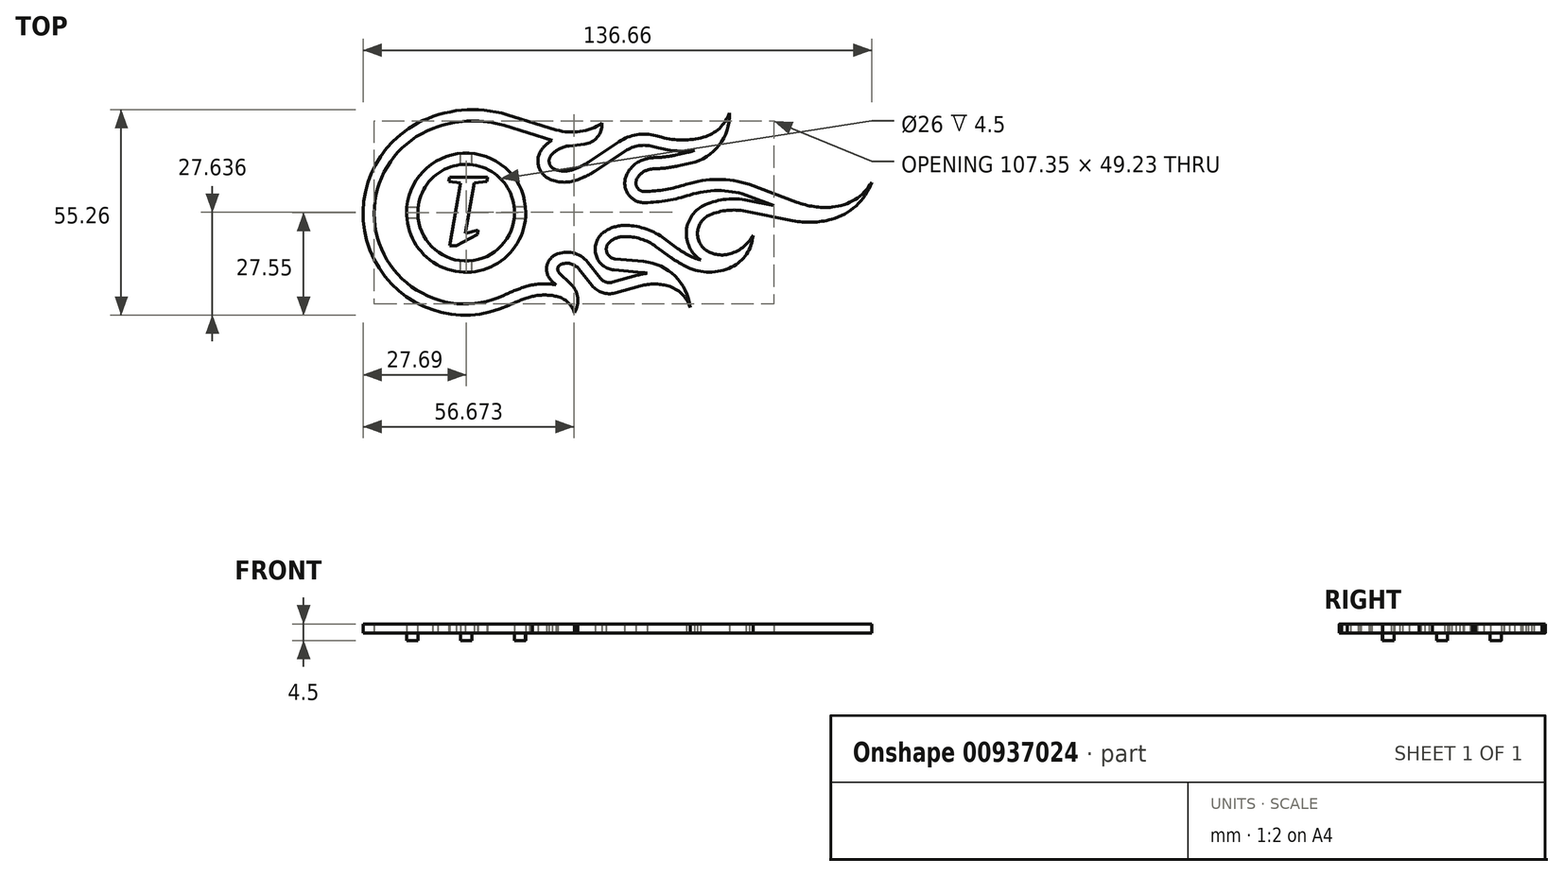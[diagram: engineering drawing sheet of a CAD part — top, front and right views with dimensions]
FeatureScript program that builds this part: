
annotation { "Feature Type Name" : "Feature", "Feature Type Description" : "" }
export const myFeature = defineFeature(function(context is Context, id is Id, definition is map)
    precondition{}
    {
        {
            var Q0;
            Q0=qCreatedBy(makeId("Top.planeOp"),FACE);
            cPlane(context, id + "F0", {"entities" : qUnion([Q0]), "cplaneType" : CPlaneType.OFFSET, "offset" : 2 * mm, "width" : 150 * mm, "height" : 150 * mm});
        }
        {
            var Q0;
            Q0=qCreatedBy(id+"F0.planeOp",FACE);
            var sketch = newSketch(context, id + "F1", { "sketchPlane" : qUnion([Q0])});
            skArc(sketch, "E0", {"start": v(-15.8, 20.8) * mm, "mid": v(-9.44, 20.3) * mm, "end": v(-3.49, 22.58) * mm});
            skLineSegment(sketch, "E1", {"start": v(-29, 24.82) * mm, "end": v(-15.8, 20.8) * mm});
            skArc(sketch, "E2", {"start": v(-53.14, 22.5) * mm, "mid": v(-64.76, -14.01) * mm, "end": v(-28.48, -26.36) * mm});
            skArc(sketch, "E3", {"start": v(-29, 24.82) * mm, "mid": v(-41.3, 26.06) * mm, "end": v(-53.14, 22.5) * mm});
            skArc(sketch, "E4", {"start": v(-8.25, 16.94) * mm, "mid": v(-4.75, 18.81) * mm, "end": v(-3.49, 22.58) * mm});
            skArc(sketch, "E5", {"start": v(-10.87, -28.44) * mm, "mid": v(-12.7, -25.58) * mm, "end": v(-15.7, -24) * mm});
            skArc(sketch, "E6", {"start": v(-15.7, -24) * mm, "mid": v(-18.94, -23.64) * mm, "end": v(-22.18, -24) * mm});
            skArc(sketch, "E7", {"start": v(-22.18, -24) * mm, "mid": v(-25.39, -25.04) * mm, "end": v(-28.48, -26.36) * mm});
            skArc(sketch, "E8", {"start": v(-10.87, -28.44) * mm, "mid": v(-10.04, -24.35) * mm, "end": v(-11.9, -20.62) * mm});
            skArc(sketch, "E9", {"start": v(-14.69, -15.51) * mm, "mid": v(-15.4, -16.45) * mm, "end": v(-15.02, -17.57) * mm});
            skLineSegment(sketch, "E10", {"start": v(-11.9, -20.62) * mm, "end": v(-15.02, -17.57) * mm});
            skArc(sketch, "E11", {"start": v(-9.7, -16.65) * mm, "mid": v(-12, -15.2) * mm, "end": v(-14.69, -15.51) * mm});
            skLineSegment(sketch, "E12", {"start": v(-9.7, -16.65) * mm, "end": v(-6.22, -21.05) * mm});
            skArc(sketch, "E13", {"start": v(-6.22, -21.05) * mm, "mid": v(-3.42, -23) * mm, "end": v(0, -23.09) * mm});
            skLineSegment(sketch, "E14", {"start": v(-8.25, 16.94) * mm, "end": v(-12.34, 16.47) * mm});
            skArc(sketch, "E15", {"start": v(-12.34, 16.47) * mm, "mid": v(-14.96, 15.66) * mm, "end": v(-17.12, 13.97) * mm});
            skArc(sketch, "E16", {"start": v(-17.12, 13.97) * mm, "mid": v(-17.66, 11.88) * mm, "end": v(-16.27, 10.22) * mm});
            skArc(sketch, "E17", {"start": v(-16.27, 10.22) * mm, "mid": v(-13.63, 9.69) * mm, "end": v(-10.98, 10.22) * mm});
            skLineSegment(sketch, "E18", {"start": v(-10.98, 10.22) * mm, "end": v(-9.42, 10.88) * mm});
            skLineSegment(sketch, "E19", {"start": v(1.1, 17.58) * mm, "end": v(-6.91, 12.23) * mm});
            skArc(sketch, "E20.filletArc", {"start": v(-9.42, 10.88) * mm, "mid": v(-8.13, 11.5) * mm, "end": v(-6.91, 12.23) * mm});
            skArc(sketch, "E21", {"start": v(10.9, 19.2) * mm, "mid": v(5.82, 19.45) * mm, "end": v(1.1, 17.58) * mm});
            skLineSegment(sketch, "E22", {"start": v(10.9, 19.2) * mm, "end": v(12.5, 18.78) * mm});
            skArc(sketch, "E23", {"start": v(12.5, 18.78) * mm, "mid": v(18.13, 18.04) * mm, "end": v(23.76, 18.78) * mm});
            skArc(sketch, "E24", {"start": v(23.76, 18.78) * mm, "mid": v(28.06, 21.17) * mm, "end": v(30.72, 25.31) * mm});
            skArc(sketch, "E25", {"start": v(20.3, 11.8) * mm, "mid": v(27.98, 16.65) * mm, "end": v(30.72, 25.31) * mm});
            skLineSegment(sketch, "E26", {"start": v(20.3, 11.8) * mm, "end": v(16.86, 11.06) * mm});
            skArc(sketch, "E27", {"start": v(10.82, 10.32) * mm, "mid": v(13.86, 10.55) * mm, "end": v(16.86, 11.06) * mm});
            skArc(sketch, "E28", {"start": v(10.82, 10.32) * mm, "mid": v(9.84, 10.23) * mm, "end": v(8.87, 10.03) * mm});
            skArc(sketch, "E29", {"start": v(8.87, 10.03) * mm, "mid": v(7.03, 9.04) * mm, "end": v(5.8, 7.34) * mm});
            skArc(sketch, "E30", {"start": v(5.8, 7.34) * mm, "mid": v(6.02, 5.16) * mm, "end": v(7.97, 4.17) * mm});
            skArc(sketch, "E31", {"start": v(19.12, 6.1) * mm, "mid": v(13.61, 4.74) * mm, "end": v(7.97, 4.17) * mm});
            skArc(sketch, "E32", {"start": v(36.14, 6.1) * mm, "mid": v(27.63, 7.44) * mm, "end": v(19.12, 6.1) * mm});
            skLineSegment(sketch, "E33", {"start": v(0, -23.09) * mm, "end": v(6.9, -21.19) * mm});
            skArc(sketch, "E34", {"start": v(14.19, -21.19) * mm, "mid": v(10.54, -20.7) * mm, "end": v(6.9, -21.19) * mm});
            skArc(sketch, "E35", {"start": v(20.17, -27.02) * mm, "mid": v(17.93, -23.33) * mm, "end": v(14.19, -21.19) * mm});
            skArc(sketch, "E36", {"start": v(20.17, -27.02) * mm, "mid": v(16.15, -18.57) * mm, "end": v(7.68, -14.62) * mm});
            skLineSegment(sketch, "E37", {"start": v(7.68, -14.62) * mm, "end": v(0, -13.91) * mm});
            skArc(sketch, "E38", {"start": v(-1.39, -9.32) * mm, "mid": v(-2.24, -12.08) * mm, "end": v(0, -13.91) * mm});
            skArc(sketch, "E39", {"start": v(2.46, -7.92) * mm, "mid": v(0.42, -8.3) * mm, "end": v(-1.39, -9.32) * mm});
            skArc(sketch, "E40", {"start": v(10.98, -10.59) * mm, "mid": v(6.94, -8.56) * mm, "end": v(2.46, -7.92) * mm});
            skLineSegment(sketch, "E41", {"start": v(10.98, -10.59) * mm, "end": v(15.06, -13.54) * mm});
            skArc(sketch, "E42", {"start": v(15.06, -13.54) * mm, "mid": v(17.16, -14.93) * mm, "end": v(19.37, -16.1) * mm});
            skArc(sketch, "E43", {"start": v(19.37, -16.1) * mm, "mid": v(25.34, -17.46) * mm, "end": v(31.3, -16.1) * mm});
            skArc(sketch, "E44", {"start": v(31.3, -16.1) * mm, "mid": v(35.34, -12.64) * mm, "end": v(37.05, -7.6) * mm});
            skArc(sketch, "E45", {"start": v(30.4, -12.7) * mm, "mid": v(34.29, -10.88) * mm, "end": v(37.05, -7.6) * mm});
            skArc(sketch, "E46", {"start": v(24.84, -11.81) * mm, "mid": v(27.53, -12.78) * mm, "end": v(30.4, -12.7) * mm});
            skArc(sketch, "E47", {"start": v(25.48, -2.1) * mm, "mid": v(22.17, -6.76) * mm, "end": v(24.84, -11.81) * mm});
            skArc(sketch, "E48", {"start": v(35.02, -1.1) * mm, "mid": v(30.17, -0.88) * mm, "end": v(25.48, -2.1) * mm});
            skLineSegment(sketch, "E49", {"start": v(35.02, -1.1) * mm, "end": v(47.7, -3.63) * mm});
            skArc(sketch, "E50", {"start": v(47.7, -3.63) * mm, "mid": v(52.94, -4.06) * mm, "end": v(58.13, -3.3) * mm});
            skArc(sketch, "E51", {"start": v(58.13, -3.3) * mm, "mid": v(64.79, 0.34) * mm, "end": v(68.97, 6.67) * mm});
            skArc(sketch, "E52", {"start": v(58.36, 0) * mm, "mid": v(64.48, 2.05) * mm, "end": v(68.97, 6.67) * mm});
            skArc(sketch, "E53", {"start": v(48.76, 1.34) * mm, "mid": v(53.49, 0.13) * mm, "end": v(58.36, 0) * mm});
            skLineSegment(sketch, "E54", {"start": v(36.14, 6.1) * mm, "end": v(48.76, 1.34) * mm});
            skArc(sketch, "E55.0", {"start": v(-29.87, 21.95) * mm, "mid": v(-38.73, 23.2) * mm, "end": v(-47.54, 21.67) * mm});
            skArc(sketch, "E56", {"start": v(-48.94, 21.12) * mm, "mid": v(-62.73, -11.25) * mm, "end": v(-29.8, -23.67) * mm});
            skLineSegment(sketch, "E57", {"start": v(-48.94, 21.12) * mm, "end": v(-47.54, 21.67) * mm});
            skLineSegment(sketch, "E58.0", {"start": v(-29.87, 21.95) * mm, "end": v(-16.92, 18) * mm});
            skArc(sketch, "E59.0", {"start": v(-12.68, 19.45) * mm, "mid": v(-12.7, 19.44) * mm, "end": v(-12.72, 19.44) * mm});
            skLineSegment(sketch, "E60", {"start": v(-16.92, 18) * mm, "end": v(-16.92, 18) * mm});
            skArc(sketch, "E61", {"start": v(-16.92, 18) * mm, "mid": v(-18.2, 17.08) * mm, "end": v(-19.34, 15.99) * mm});
            skArc(sketch, "E62.0", {"start": v(-19.37, 15.96) * mm, "mid": v(-20.58, 11.21) * mm, "end": v(-17.43, 7.46) * mm});
            skArc(sketch, "E63.0", {"start": v(-17.43, 7.46) * mm, "mid": v(-13.63, 6.69) * mm, "end": v(-9.82, 7.46) * mm});
            skLineSegment(sketch, "E64.0", {"start": v(-9.82, 7.46) * mm, "end": v(-8.25, 8.12) * mm});
            skArc(sketch, "E65.0", {"start": v(-8.25, 8.12) * mm, "mid": v(-6.71, 8.86) * mm, "end": v(-5.25, 9.74) * mm});
            skLineSegment(sketch, "E66.0", {"start": v(2.76, 15.09) * mm, "end": v(-5.25, 9.74) * mm});
            skArc(sketch, "E67.0", {"start": v(10.13, 16.3) * mm, "mid": v(6.31, 16.5) * mm, "end": v(2.76, 15.09) * mm});
            skLineSegment(sketch, "E68.0", {"start": v(10.13, 16.3) * mm, "end": v(11.74, 15.88) * mm});
            skArc(sketch, "E69.0", {"start": v(11.74, 15.88) * mm, "mid": v(16.51, 15.1) * mm, "end": v(21.35, 15.25) * mm});
            skLineSegment(sketch, "E70.0", {"start": v(19.3, 14.65) * mm, "end": v(16.22, 13.99) * mm});
            skArc(sketch, "E71.0", {"start": v(19.66, 14.73) * mm, "mid": v(20.52, 14.95) * mm, "end": v(21.35, 15.25) * mm});
            skArc(sketch, "E72.0", {"start": v(10.73, 13.32) * mm, "mid": v(13.5, 13.53) * mm, "end": v(16.22, 13.99) * mm});
            skArc(sketch, "E73.0", {"start": v(10.73, 13.32) * mm, "mid": v(9.4, 13.2) * mm, "end": v(8.08, 12.92) * mm});
            skArc(sketch, "E74.0", {"start": v(8.08, 12.92) * mm, "mid": v(5.05, 11.3) * mm, "end": v(3.04, 8.52) * mm});
            skArc(sketch, "E75.0", {"start": v(3.04, 8.52) * mm, "mid": v(3.54, 3.47) * mm, "end": v(8.07, 1.17) * mm});
            skArc(sketch, "E76.0", {"start": v(20.04, 3.25) * mm, "mid": v(14.12, 1.79) * mm, "end": v(8.07, 1.17) * mm});
            skLineSegment(sketch, "E77.0", {"start": v(35.6, 1.84) * mm, "end": v(42.66, 0.43) * mm});
            skArc(sketch, "E78.0", {"start": v(35.6, 1.84) * mm, "mid": v(29.87, 2.1) * mm, "end": v(24.3, 0.67) * mm});
            skArc(sketch, "E79.0", {"start": v(24.3, 0.67) * mm, "mid": v(19.19, -6.38) * mm, "end": v(23, -14.2) * mm});
            skArc(sketch, "E80.0", {"start": v(20.66, -13.4) * mm, "mid": v(21.81, -13.87) * mm, "end": v(23, -14.2) * mm});
            skArc(sketch, "E81.0", {"start": v(16.82, -11.12) * mm, "mid": v(18.69, -12.35) * mm, "end": v(20.66, -13.4) * mm});
            skLineSegment(sketch, "E82.0", {"start": v(12.74, -8.16) * mm, "end": v(16.82, -11.12) * mm});
            skArc(sketch, "E83.0", {"start": v(12.74, -8.16) * mm, "mid": v(7.83, -5.7) * mm, "end": v(2.4, -4.92) * mm});
            skArc(sketch, "E84.0", {"start": v(2.4, -4.92) * mm, "mid": v(-0.61, -5.48) * mm, "end": v(-3.28, -7) * mm});
            skArc(sketch, "E85.0", {"start": v(-3.28, -7) * mm, "mid": v(-5.11, -12.95) * mm, "end": v(-0.28, -16.9) * mm});
            skLineSegment(sketch, "E86.0", {"start": v(7.4, -17.6) * mm, "end": v(-0.28, -16.9) * mm});
            skLineSegment(sketch, "E87.0", {"start": v(-0.8, -20.2) * mm, "end": v(6.1, -18.3) * mm});
            skArc(sketch, "E88", {"start": v(8.67, -17.8) * mm, "mid": v(8.04, -17.68) * mm, "end": v(7.4, -17.6) * mm});
            skArc(sketch, "E89", {"start": v(8.67, -17.8) * mm, "mid": v(7.38, -18) * mm, "end": v(6.1, -18.3) * mm});
            skArc(sketch, "E90.0", {"start": v(-3.87, -19.2) * mm, "mid": v(-2.48, -20.16) * mm, "end": v(-0.8, -20.2) * mm});
            skLineSegment(sketch, "E91.0", {"start": v(-7.35, -14.8) * mm, "end": v(-3.87, -19.2) * mm});
            skArc(sketch, "E92.0", {"start": v(-7.35, -14.8) * mm, "mid": v(-11.32, -12.28) * mm, "end": v(-16, -12.81) * mm});
            skArc(sketch, "E93.0", {"start": v(-16, -12.81) * mm, "mid": v(-18.35, -15.97) * mm, "end": v(-17.12, -19.72) * mm});
            skLineSegment(sketch, "E94.0", {"start": v(-15.9, -20.9) * mm, "end": v(-17.12, -19.72) * mm});
            skArc(sketch, "E95.0", {"start": v(-15.9, -20.9) * mm, "mid": v(-19.4, -20.64) * mm, "end": v(-22.86, -21.08) * mm});
            skArc(sketch, "E96.0", {"start": v(-22.98, -21.11) * mm, "mid": v(-26.29, -22.18) * mm, "end": v(-29.49, -23.52) * mm});
            skLineSegment(sketch, "E97", {"start": v(-22.98, -21.11) * mm, "end": v(-22.86, -21.08) * mm});
            skLineSegment(sketch, "E98", {"start": v(19.3, 14.65) * mm, "end": v(19.66, 14.73) * mm});
            skLineSegment(sketch, "E99", {"start": v(-19.37, 15.96) * mm, "end": v(-19.34, 15.99) * mm});
            skArc(sketch, "E100", {"start": v(35.15, 3.27) * mm, "mid": v(27.6, 4.44) * mm, "end": v(20.04, 3.25) * mm});
            skLineSegment(sketch, "E101", {"start": v(35.15, 3.27) * mm, "end": v(42.66, 0.43) * mm});
            skLineSegment(sketch, "E102", {"start": v(-29.8, -23.67) * mm, "end": v(-29.49, -23.52) * mm});
            skSolve(sketch);
        }
        {
            var Q0;
            Q0=qSketchRegion(id+"F1",true);
            extrude(context, id + "F2", {"entities" : qUnion([Q0]), "depth" : 2.5 * mm, "offsetDistance" : 25 * mm});
        }
        {
            var Q0;
            Q0=qCreatedBy(makeId("Top.planeOp"),FACE);
            var sketch = newSketch(context, id + "F3", { "sketchPlane" : qUnion([Q0])});
            skCircle(sketch, "E103", {"center": v(-40, -1.5) * mm, "radius": 16 * mm});
            skCircle(sketch, "E104", {"center": v(-40, -1.5) * mm, "radius": 13 * mm});
            skSolve(sketch);
        }
        {
            var Q0;
            Q0=qSketchRegion(id+"F3",true);
            extrude(context, id + "F4", {"entities" : qUnion([Q0]), "operationType" : NewBodyOperationType.ADD, "depth" : 4.5 * mm, "offsetDistance" : 25 * mm});
        }
        {
            var Q0;
            Q0=qCreatedBy(id+"F0.planeOp",FACE);
            var sketch = newSketch(context, id + "F5", { "sketchPlane" : qUnion([Q0])});
            skText(sketch, "E105", { "text": "1", "fontName": "Tinos-BoldItalic.ttf"});
            const initialGuessF5  = {"E105": [-0.0336, 0.008, -1, 0, 0.02]};
            skSetInitialGuess(sketch, initialGuessF5);
            skSolve(sketch);
        }
        {
            var Q0;
            Q0=qSketchRegion(id+"F5",true);
            extrude(context, id + "F6", {"entities" : qUnion([Q0]), "depth" : 2.5 * mm, "offsetDistance" : 25 * mm});
        }
        {
            var Q0;
            Q0=qCreatedBy(makeId("Top.planeOp"),FACE);
            var sketch = newSketch(context, id + "F7", { "sketchPlane" : qUnion([Q0])});
            skArc(sketch, "E106", {"start": v(-38.5, -17.43) * mm, "mid": v(-28.69, -12.81) * mm, "end": v(-24.07, -3) * mm});
            skArc(sketch, "E107", {"start": v(-38.5, -14.41) * mm, "mid": v(-30.8, -10.7) * mm, "end": v(-27.09, -3) * mm});
            skArc(sketch, "E108", {"start": v(-27.09, 0) * mm, "mid": v(-30.8, 7.7) * mm, "end": v(-38.5, 11.41) * mm});
            skArc(sketch, "E109", {"start": v(-24.07, 0) * mm, "mid": v(-28.69, 9.81) * mm, "end": v(-38.5, 14.43) * mm});
            skArc(sketch, "E110", {"start": v(-52.91, -3) * mm, "mid": v(-49.2, -10.7) * mm, "end": v(-41.5, -14.41) * mm});
            skArc(sketch, "E111", {"start": v(-55.93, -3) * mm, "mid": v(-51.31, -12.81) * mm, "end": v(-41.5, -17.43) * mm});
            skArc(sketch, "E112", {"start": v(-41.5, 14.43) * mm, "mid": v(-51.31, 9.81) * mm, "end": v(-55.93, 0) * mm});
            skArc(sketch, "E113", {"start": v(-41.5, 11.41) * mm, "mid": v(-49.19, 7.7) * mm, "end": v(-52.91, 0.02) * mm});
            skLineSegment(sketch, "E114", {"start": v(-41.5, -17.43) * mm, "end": v(-41.5, -14.41) * mm});
            skLineSegment(sketch, "E115", {"start": v(-38.5, -17.43) * mm, "end": v(-38.5, -14.41) * mm});
            skLineSegment(sketch, "E116", {"start": v(-27.09, -3) * mm, "end": v(-24.07, -3) * mm});
            skLineSegment(sketch, "E117", {"start": v(-24.07, 0) * mm, "end": v(-27.09, 0) * mm});
            skLineSegment(sketch, "E118", {"start": v(-38.5, 11.41) * mm, "end": v(-38.5, 14.43) * mm});
            skLineSegment(sketch, "E119", {"start": v(-41.5, 11.41) * mm, "end": v(-41.5, 14.43) * mm});
            skLineSegment(sketch, "E120", {"start": v(-52.91, -3) * mm, "end": v(-55.93, -3) * mm});
            skLineSegment(sketch, "E121", {"start": v(-55.93, 0) * mm, "end": v(-52.91, 0.02) * mm});
            skSolve(sketch);
        }
        {
            var Q0;
            Q0=qSketchRegion(id+"F7",true);
            extrude(context, id + "F8", {"entities" : qUnion([Q0]), "operationType" : NewBodyOperationType.REMOVE, "depth" : 2 * mm, "offsetDistance" : 25 * mm});
        }
    });
